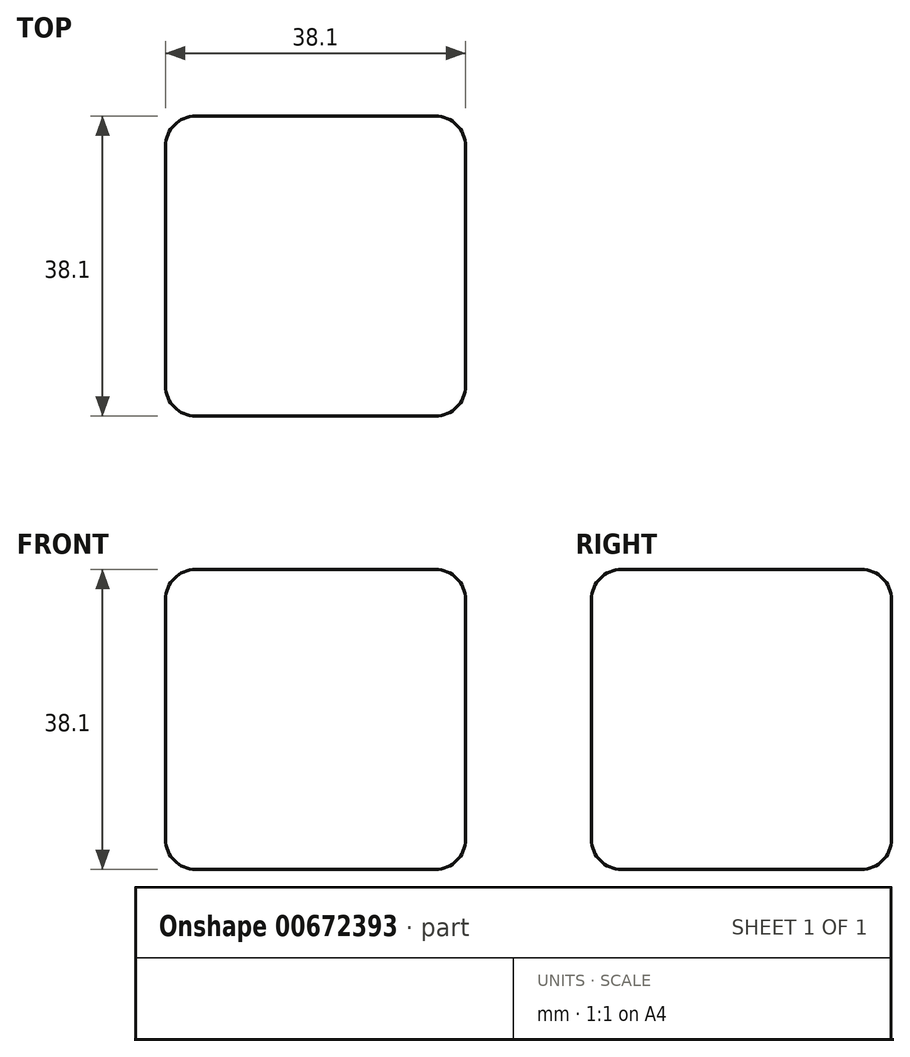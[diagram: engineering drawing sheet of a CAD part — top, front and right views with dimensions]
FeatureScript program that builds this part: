
annotation { "Feature Type Name" : "Feature", "Feature Type Description" : "" }
export const myFeature = defineFeature(function(context is Context, id is Id, definition is map)
    precondition{}
    {
        {
            var Q0;
            Q0=qCreatedBy(makeId("Front.planeOp"),FACE);
            var sketch = newSketch(context, id + "F0", { "sketchPlane" : qUnion([Q0])});
            skLineSegment(sketch, "E0.bottom", {"start": v(-25.58, 41.26) * mm, "end": v(12.52, 41.26) * mm});
            skLineSegment(sketch, "E0.top", {"start": v(-25.58, 3.16) * mm, "end": v(12.52, 3.16) * mm});
            skLineSegment(sketch, "E0.left", {"start": v(-25.58, 41.26) * mm, "end": v(-25.58, 3.16) * mm});
            skLineSegment(sketch, "E0.right", {"start": v(12.52, 41.26) * mm, "end": v(12.52, 3.16) * mm});
            skSolve(sketch);
        }
        {
            var Q0;
            Q0=makeQuery(id+"F0.imprint","IMPRINT",FACE,{"disambiguationData":[TD([[makeQuery(id+"F0.imprint","IMPRINT",EDGE,{"derivedFrom":sQuery(id+"F0.wireOp",EDGE,"E0.bottom")}),-1.0]])]});
            extrude(context, id + "F1", {"entities" : qUnion([Q0]), "depth" : 38.1 * mm, "offsetDistance" : 25.4 * mm});
        }
        {
            var Q0;
            Q0=makeQuery(id+"F1.opExtrude","CAP_EDGE",EDGE,{"disambiguationData":[OSD([sQuery(id+"F0.wireOp",EDGE,"E0.bottom")])],"isStart":false});
            var Q1;
            Q1=makeQuery(id+"F1.opExtrude","SWEPT_EDGE",EDGE,{"disambiguationData":[OSD([sQuery(id+"F0.wireOp",EDGE,"E0.bottom"),sQuery(id+"F0.wireOp",EDGE,"E0.right")])]});
            var Q2;
            Q2=makeQuery(id+"F1.opExtrude","CAP_EDGE",EDGE,{"disambiguationData":[OSD([sQuery(id+"F0.wireOp",EDGE,"E0.right")])],"isStart":false});
            var Q3;
            Q3=makeQuery(id+"F1.opExtrude","CAP_EDGE",EDGE,{"disambiguationData":[OSD([sQuery(id+"F0.wireOp",EDGE,"E0.top")])],"isStart":false});
            var Q4;
            Q4=makeQuery(id+"F1.opExtrude","CAP_EDGE",EDGE,{"disambiguationData":[OSD([sQuery(id+"F0.wireOp",EDGE,"E0.left")])],"isStart":false});
            var Q5;
            Q5=makeQuery(id+"F1.opExtrude","SWEPT_EDGE",EDGE,{"disambiguationData":[OSD([sQuery(id+"F0.wireOp",EDGE,"E0.bottom"),sQuery(id+"F0.wireOp",EDGE,"E0.left")])]});
            var Q6;
            Q6=makeQuery(id+"F1.opExtrude","CAP_EDGE",EDGE,{"disambiguationData":[OSD([sQuery(id+"F0.wireOp",EDGE,"E0.bottom")])],"isStart":true});
            var Q7;
            Q7=makeQuery(id+"F1.opExtrude","SWEPT_EDGE",EDGE,{"disambiguationData":[OSD([sQuery(id+"F0.wireOp",EDGE,"E0.top"),sQuery(id+"F0.wireOp",EDGE,"E0.right")])]});
            var Q8;
            Q8=makeQuery(id+"F1.opExtrude","CAP_EDGE",EDGE,{"disambiguationData":[OSD([sQuery(id+"F0.wireOp",EDGE,"E0.right")])],"isStart":true});
            var Q9;
            Q9=makeQuery(id+"F1.opExtrude","CAP_EDGE",EDGE,{"disambiguationData":[OSD([sQuery(id+"F0.wireOp",EDGE,"E0.top")])],"isStart":true});
            var Q10;
            Q10=makeQuery(id+"F1.opExtrude","CAP_EDGE",EDGE,{"disambiguationData":[OSD([sQuery(id+"F0.wireOp",EDGE,"E0.left")])],"isStart":true});
            var Q11;
            Q11=makeQuery(id+"F1.opExtrude","SWEPT_EDGE",EDGE,{"disambiguationData":[OSD([sQuery(id+"F0.wireOp",EDGE,"E0.top"),sQuery(id+"F0.wireOp",EDGE,"E0.left")])]});
            fillet(context, id + "F2", {"entities" : qUnion([Q0, Q1, Q2, Q3, Q4, Q5, Q6, Q7, Q8, Q9, Q10, Q11]), "radius" : 3.8 * mm, "tangentPropagation" : true, "allowEdgeOverflow" : false});
        }
    });
